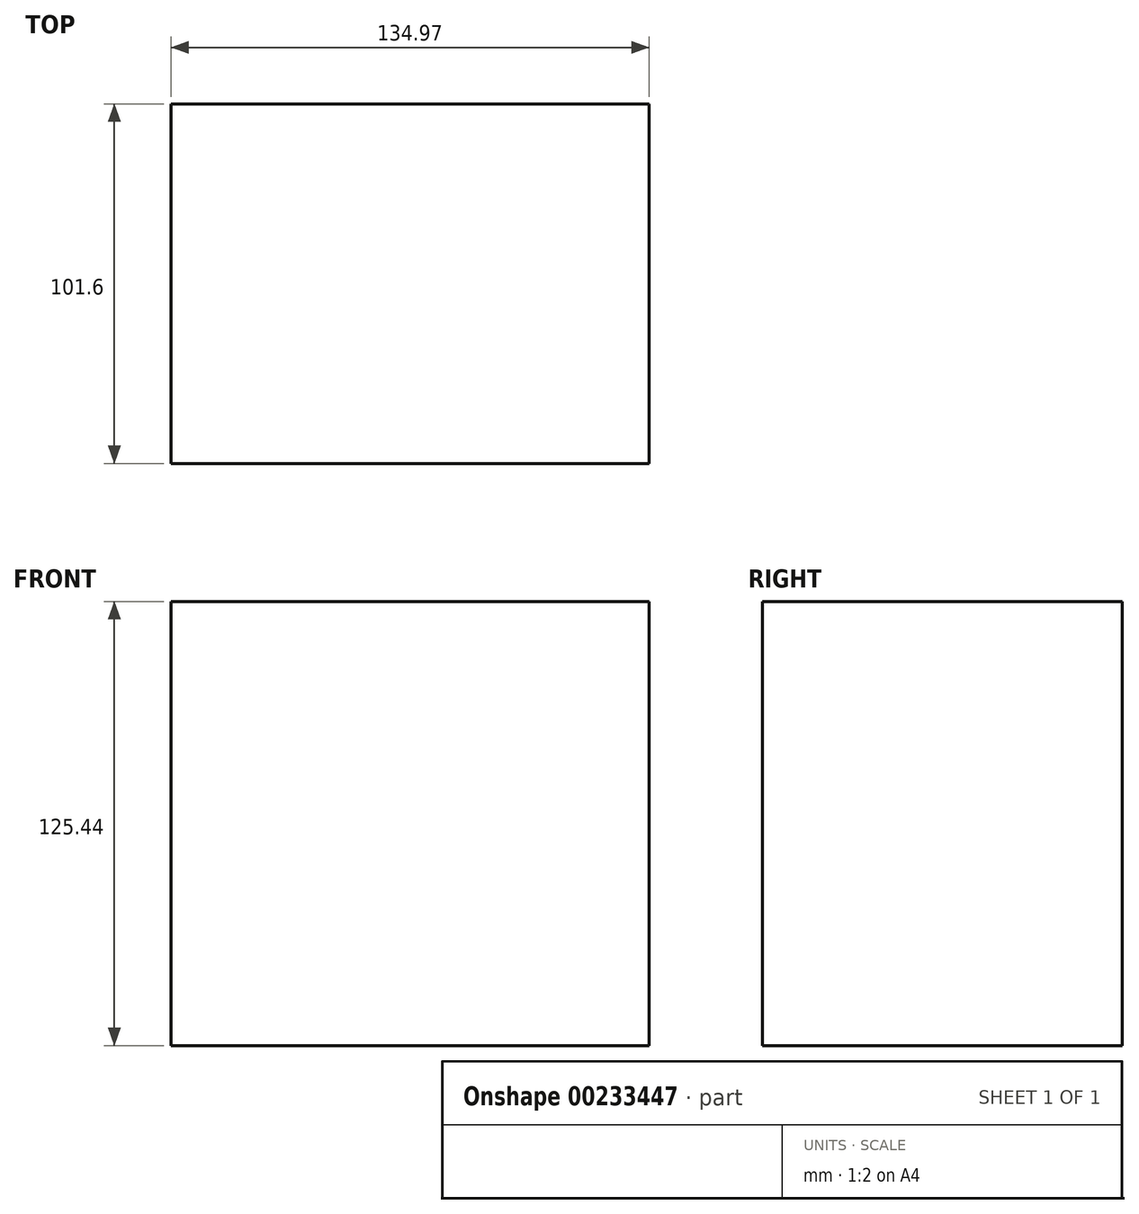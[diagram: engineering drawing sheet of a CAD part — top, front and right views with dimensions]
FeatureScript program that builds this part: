
annotation { "Feature Type Name" : "Feature", "Feature Type Description" : "" }
export const myFeature = defineFeature(function(context is Context, id is Id, definition is map)
    precondition{}
    {
        {
            var Q0;
            Q0=qCreatedBy(makeId("Front.planeOp"),FACE);
            var sketch = newSketch(context, id + "F0", { "sketchPlane" : qUnion([Q0])});
            skLineSegment(sketch, "E0.bottom", {"start": v(0, 0) * mm, "end": v(134.97, 0) * mm});
            skLineSegment(sketch, "E0.top", {"start": v(0, 125.44) * mm, "end": v(134.97, 125.44) * mm});
            skLineSegment(sketch, "E0.left", {"start": v(0, 0) * mm, "end": v(0, 125.44) * mm});
            skLineSegment(sketch, "E0.right", {"start": v(134.97, 0) * mm, "end": v(134.97, 125.44) * mm});
            skSolve(sketch);
        }
        {
            var Q0;
            Q0=makeQuery(id+"F0.imprint","IMPRINT",FACE,{"disambiguationData":[TD([[makeQuery(id+"F0.imprint","IMPRINT",EDGE,{"derivedFrom":sQuery(id+"F0.wireOp",EDGE,"E0.bottom")}),1.0]])]});
            extrude(context, id + "F1", {"entities" : qUnion([Q0]), "depth" : 101.6 * mm});
        }
    });
